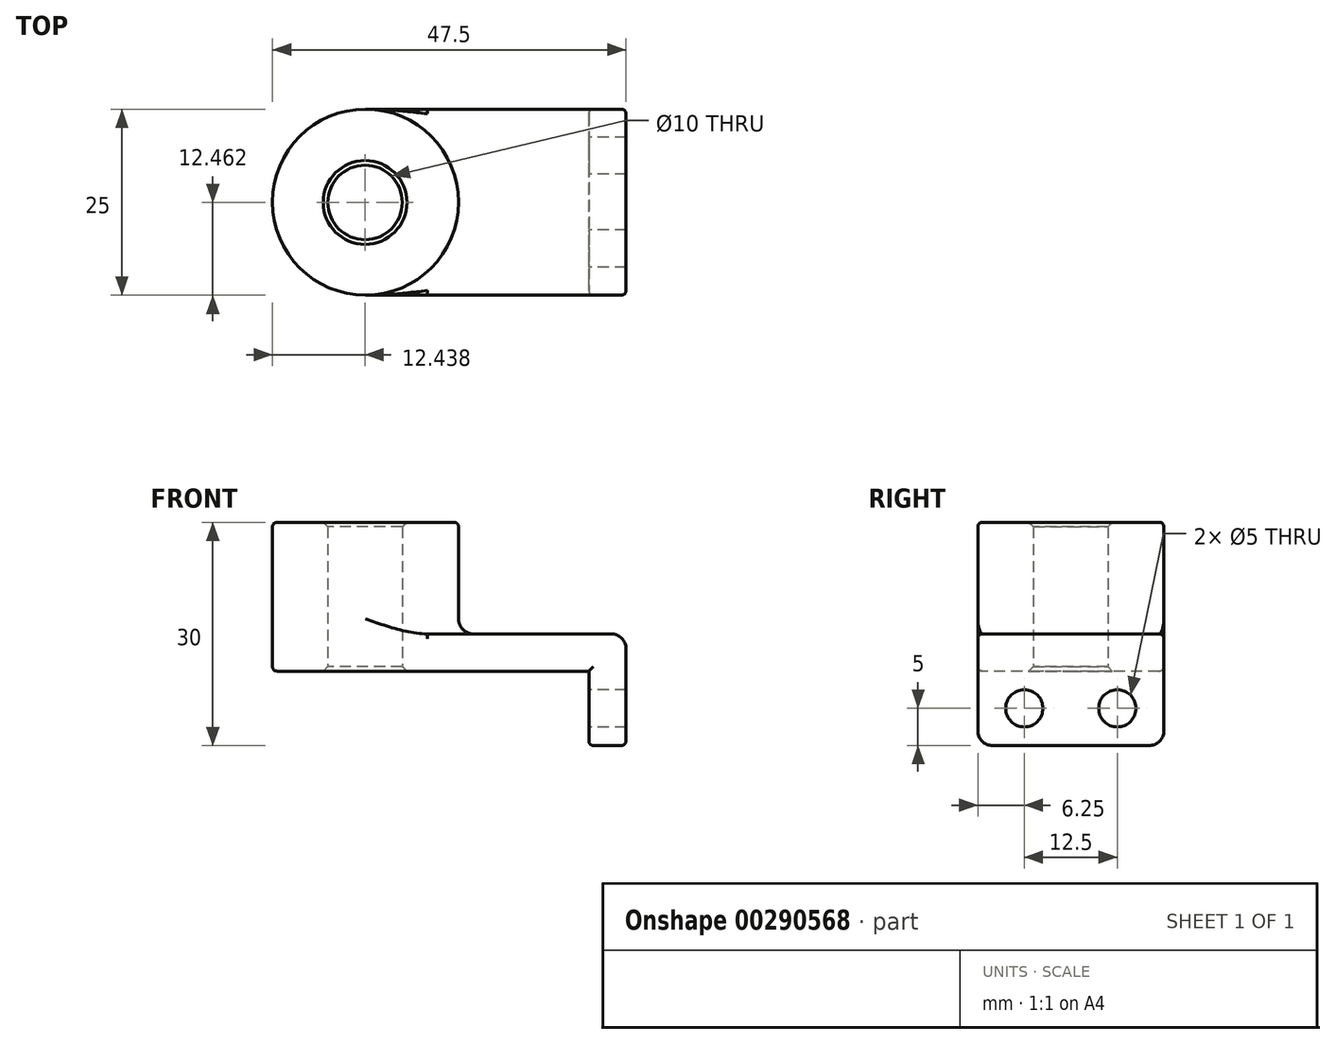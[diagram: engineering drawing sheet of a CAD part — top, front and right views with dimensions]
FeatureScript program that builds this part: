
annotation { "Feature Type Name" : "Feature", "Feature Type Description" : "" }
export const myFeature = defineFeature(function(context is Context, id is Id, definition is map)
    precondition{}
    {
        {
            var Q0;
            Q0=qCreatedBy(makeId("Top.planeOp"),FACE);
            var sketch = newSketch(context, id + "F0", { "sketchPlane" : qUnion([Q0])});
            skLineSegment(sketch, "E0.bottom", {"start": v(15, 12.5) * mm, "end": v(-15, 12.5) * mm});
            skLineSegment(sketch, "E0.top", {"start": v(15, -12.5) * mm, "end": v(-15, -12.5) * mm});
            skLineSegment(sketch, "E0.left", {"start": v(15, 12.5) * mm, "end": v(15, -12.5) * mm});
            skLineSegment(sketch, "E0.right", {"start": v(-15, 12.5) * mm, "end": v(-15, -12.5) * mm});
            skPoint(sketch, "E0.middle", {"position": v(0, 0) * mm});
            skCircle(sketch, "E1", {"center": v(-15, 0) * mm, "radius": 12.5 * mm});
            skCircle(sketch, "E2", {"center": v(-15.06, -0.04) * mm, "radius": 5 * mm});
            skSolve(sketch);
        }
        {
            var Q0;
            {var subQ1=sQuery(id+"F0.wireOp",EDGE,"E0.right");var subQ3=sQuery(id+"F0.wireOp",EDGE,"E2");var subQ4=makeQuery(id+"F0.imprint","INTERSECT",VERTEX,{"disambiguationData":[OD(0.0)],"derivedFrom":[subQ1,subQ3]});Q0=makeQuery(id+"F0.imprint","IMPRINT",FACE,{"disambiguationData":[TD([[makeQuery(id+"F0.imprint","IMPRINT",EDGE,{"disambiguationData":[TD([[subQ4,-1.0]])],"derivedFrom":subQ3}),-1.0]])]});}
            var Q1;
            {var subQ1=sQuery(id+"F0.wireOp",EDGE,"E0.right");var subQ3=sQuery(id+"F0.wireOp",EDGE,"E2");var subQ4=makeQuery(id+"F0.imprint","INTERSECT",VERTEX,{"disambiguationData":[OD(0.0)],"derivedFrom":[subQ1,subQ3]});Q1=makeQuery(id+"F0.imprint","IMPRINT",FACE,{"disambiguationData":[TD([[makeQuery(id+"F0.imprint","IMPRINT",EDGE,{"disambiguationData":[TD([[subQ4,1.0]])],"derivedFrom":subQ3}),-1.0]])]});}
            var Q2;
            {var subQ0=sQuery(id+"F0.wireOp",EDGE,"E0.bottom");Q2=makeQuery(id+"F0.imprint","IMPRINT",FACE,{"disambiguationData":[TD([[makeQuery(id+"F0.imprint","IMPRINT",EDGE,{"derivedFrom":subQ0}),1.0]])]});}
            extrude(context, id + "F1", {"entities" : qUnion([Q0, Q1, Q2]), "depth" : 5 * mm});
        }
        {
            var Q0;
            {var subQ1=sQuery(id+"F0.wireOp",EDGE,"E0.right");var subQ3=sQuery(id+"F0.wireOp",EDGE,"E2");var subQ4=makeQuery(id+"F0.imprint","INTERSECT",VERTEX,{"disambiguationData":[OD(0.0)],"derivedFrom":[subQ1,subQ3]});Q0=makeQuery(id+"F0.imprint","IMPRINT",FACE,{"disambiguationData":[TD([[makeQuery(id+"F0.imprint","IMPRINT",EDGE,{"disambiguationData":[TD([[subQ4,1.0]])],"derivedFrom":subQ3}),-1.0]])]});}
            var Q1;
            {var subQ1=sQuery(id+"F0.wireOp",EDGE,"E0.right");var subQ3=sQuery(id+"F0.wireOp",EDGE,"E2");var subQ4=makeQuery(id+"F0.imprint","INTERSECT",VERTEX,{"disambiguationData":[OD(0.0)],"derivedFrom":[subQ1,subQ3]});Q1=makeQuery(id+"F0.imprint","IMPRINT",FACE,{"disambiguationData":[TD([[makeQuery(id+"F0.imprint","IMPRINT",EDGE,{"disambiguationData":[TD([[subQ4,-1.0]])],"derivedFrom":subQ3}),-1.0]])]});}
            extrude(context, id + "F2", {"entities" : qUnion([Q0, Q1]), "operationType" : NewBodyOperationType.ADD, "depth" : 20 * mm});
        }
        {
            var Q0;
            Q0=makeQuery(id+"F1.opExtrude","SWEPT_FACE",FACE,{"disambiguationData":[OSD([sQuery(id+"F0.wireOp",EDGE,"E0.left")])]});
            var sketch = newSketch(context, id + "F3", { "sketchPlane" : qUnion([Q0])});
            skPoint(sketch, "E3.oppositeSnap0", {"position": v(12.5, 2.5) * mm});
            skLineSegment(sketch, "E3.bottom", {"start": v(-12.5, 5) * mm, "end": v(12.5, 5) * mm});
            skLineSegment(sketch, "E3.top", {"start": v(-12.5, -10) * mm, "end": v(12.5, -10) * mm});
            skLineSegment(sketch, "E3.left", {"start": v(-12.5, 5) * mm, "end": v(-12.5, -10) * mm});
            skLineSegment(sketch, "E3.right", {"start": v(12.5, 5) * mm, "end": v(12.5, -10) * mm});
            skLineSegment(sketch, "E4", {"start": v(0, 5) * mm, "end": v(0, -10) * mm});
            skPoint(sketch, "E4.startSnap0", {"position": v(0, 5) * mm});
            skPoint(sketch, "E4.startSnap1", {"position": v(0, 5) * mm});
            skPoint(sketch, "E4.endSnap0", {"position": v(0, 5) * mm});
            skCircle(sketch, "E5", {"center": v(-6.25, -5) * mm, "radius": 2.5 * mm});
            skCircle(sketch, "E6.MirrorC", {"center": v(6.25, -5) * mm, "radius": 2.5 * mm});
            skSolve(sketch);
        }
        {
            var Q0;
            {var subQ5=sQuery(id+"F3.wireOp",EDGE,"E3.top");var subQ8=sQuery(id+"F3.wireOp",EDGE,"E3.left");var subQ10=makeQuery(id+"F3.imprint","INTERSECT",VERTEX,{"derivedFrom":[subQ5,subQ8]});Q0=makeQuery(id+"F3.imprint","IMPRINT",FACE,{"disambiguationData":[TD([[makeQuery(id+"F3.imprint","IMPRINT",EDGE,{"disambiguationData":[TD([[subQ10,-1.0]])],"derivedFrom":subQ5}),1.0]])]});}
            var Q1;
            {var subQ1=sQuery(id+"F3.wireOp",EDGE,"E3.bottom");var subQ8=sQuery(id+"F3.wireOp",EDGE,"E3.left");var subQ10=makeQuery(id+"F3.imprint","INTERSECT",VERTEX,{"derivedFrom":[subQ1,subQ8]});Q1=makeQuery(id+"F3.imprint","IMPRINT",FACE,{"disambiguationData":[TD([[makeQuery(id+"F3.imprint","IMPRINT",EDGE,{"disambiguationData":[TD([[subQ10,1.0]])],"derivedFrom":subQ1}),1.0]])]});}
            var Q2;
            {var subQ5=sQuery(id+"F3.wireOp",EDGE,"E3.bottom");var subQ8=sQuery(id+"F3.wireOp",EDGE,"E3.right");var subQ10=makeQuery(id+"F3.imprint","INTERSECT",VERTEX,{"derivedFrom":[subQ5,subQ8]});Q2=makeQuery(id+"F3.imprint","IMPRINT",FACE,{"disambiguationData":[TD([[makeQuery(id+"F3.imprint","IMPRINT",EDGE,{"disambiguationData":[TD([[subQ10,-1.0]])],"derivedFrom":subQ5}),1.0]])]});}
            var Q3;
            {var subQ5=sQuery(id+"F3.wireOp",EDGE,"E3.top");var subQ8=sQuery(id+"F3.wireOp",EDGE,"E3.right");var subQ10=makeQuery(id+"F3.imprint","INTERSECT",VERTEX,{"derivedFrom":[subQ5,subQ8]});Q3=makeQuery(id+"F3.imprint","IMPRINT",FACE,{"disambiguationData":[TD([[makeQuery(id+"F3.imprint","IMPRINT",EDGE,{"disambiguationData":[TD([[subQ10,1.0]])],"derivedFrom":subQ5}),1.0]])]});}
            extrude(context, id + "F4", {"entities" : qUnion([Q0, Q1, Q2, Q3]), "operationType" : NewBodyOperationType.ADD, "depth" : 5 * mm});
        }
        {
            var Q0;
            {var subQ0=sQuery(id+"F0.wireOp",EDGE,"E1");Q0=makeQuery(id+"F2.boolean.opBoolean","INTERSECT",EDGE,{"derivedFrom":[makeQuery(id+"F1.opExtrude","CAP_FACE",FACE,{"disambiguationData":[OSD([sQuery(id+"F0.wireOp",EDGE,"E0.bottom"),sQuery(id+"F0.wireOp",EDGE,"E0.top"),sQuery(id+"F0.wireOp",EDGE,"E0.left"),subQ0,sQuery(id+"F0.wireOp",EDGE,"E2")])],"isStart":false}),makeQuery(id+"F2.opExtrude","SWEPT_FACE",FACE,{"disambiguationData":[OSD([subQ0])]})]});}
            var Q1;
            Q1=makeQuery(id+"F4.opExtrude","CAP_EDGE",EDGE,{"disambiguationData":[OSD([sQuery(id+"F3.wireOp",EDGE,"E3.bottom")])],"isStart":false});
            var Q2;
            Q2=makeQuery(id+"F4.opExtrude","SWEPT_EDGE",EDGE,{"disambiguationData":[OSD([sQuery(id+"F3.wireOp",EDGE,"E3.top"),sQuery(id+"F3.wireOp",EDGE,"E3.left")])]});
            var Q3;
            Q3=makeQuery(id+"F4.opExtrude","SWEPT_EDGE",EDGE,{"disambiguationData":[OSD([sQuery(id+"F3.wireOp",EDGE,"E3.top"),sQuery(id+"F3.wireOp",EDGE,"E3.right")])]});
            var Q4;
            Q4=makeQuery(id+"F1.opExtrude","CAP_EDGE",EDGE,{"disambiguationData":[OSD([sQuery(id+"F0.wireOp",EDGE,"E0.left")])],"isStart":true});
            fillet(context, id + "F5", {"entities" : qUnion([Q0, Q1, Q2, Q3, Q4]), "radius" : 2 * mm, "tangentPropagation" : true, "allowEdgeOverflow" : false});
        }
        {
            var Q0;
            Q0=makeQuery(id+"F4.boolean.opBoolean","MERGE",EDGE,{"derivedFrom":[makeQuery(id+"F1.opExtrude","CAP_EDGE",EDGE,{"disambiguationData":[OSD([sQuery(id+"F0.wireOp",EDGE,"E0.top")])],"isStart":false}),makeQuery(id+"F4.opExtrude","SWEPT_EDGE",EDGE,{"disambiguationData":[OSD([sQuery(id+"F3.wireOp",EDGE,"E3.bottom"),sQuery(id+"F3.wireOp",EDGE,"E3.left")])]})]});
            var Q1;
            Q1=makeQuery(id+"F1.opExtrude","CAP_EDGE",EDGE,{"disambiguationData":[OSD([sQuery(id+"F0.wireOp",EDGE,"E0.top")])],"isStart":true});
            var Q2;
            Q2=makeQuery(id+"F4.opExtrude","CAP_EDGE",EDGE,{"disambiguationData":[OSD([sQuery(id+"F3.wireOp",EDGE,"E3.left")])],"isStart":false});
            var Q3;
            Q3=makeQuery(id+"F5.opFillet","BLEND_EDGE",EDGE,{"blendedFrom":[makeQuery(id+"F4.opExtrude","CAP_EDGE",EDGE,{"disambiguationData":[OSD([sQuery(id+"F3.wireOp",EDGE,"E3.bottom")])],"isStart":false}),makeQuery(id+"F4.boolean.opBoolean","MERGE",FACE,{"derivedFrom":[makeQuery(id+"F1.opExtrude","SWEPT_FACE",FACE,{"disambiguationData":[OSD([sQuery(id+"F0.wireOp",EDGE,"E0.top")])]}),makeQuery(id+"F4.opExtrude","SWEPT_FACE",FACE,{"disambiguationData":[OSD([sQuery(id+"F3.wireOp",EDGE,"E3.left")])]})]})],"blendedInto":[makeQuery(id+"F4.boolean.opBoolean","MERGE",FACE,{"derivedFrom":[makeQuery(id+"F1.opExtrude","SWEPT_FACE",FACE,{"disambiguationData":[OSD([sQuery(id+"F0.wireOp",EDGE,"E0.top")])]}),makeQuery(id+"F4.opExtrude","SWEPT_FACE",FACE,{"disambiguationData":[OSD([sQuery(id+"F3.wireOp",EDGE,"E3.left")])]})]})]});
            var Q4;
            Q4=makeQuery(id+"F4.opExtrude","CAP_EDGE",EDGE,{"disambiguationData":[OSD([sQuery(id+"F3.wireOp",EDGE,"E3.left")])],"isStart":true});
            var Q5;
            Q5=makeQuery(id+"F5.opFillet","BLEND_EDGE",EDGE,{"blendedFrom":[makeQuery(id+"F1.opExtrude","CAP_EDGE",EDGE,{"disambiguationData":[OSD([sQuery(id+"F0.wireOp",EDGE,"E0.left")])],"isStart":true}),makeQuery(id+"F4.boolean.opBoolean","MERGE",FACE,{"derivedFrom":[makeQuery(id+"F1.opExtrude","SWEPT_FACE",FACE,{"disambiguationData":[OSD([sQuery(id+"F0.wireOp",EDGE,"E0.top")])]}),makeQuery(id+"F4.opExtrude","SWEPT_FACE",FACE,{"disambiguationData":[OSD([sQuery(id+"F3.wireOp",EDGE,"E3.left")])]})]})],"blendedInto":[makeQuery(id+"F4.boolean.opBoolean","MERGE",FACE,{"derivedFrom":[makeQuery(id+"F1.opExtrude","SWEPT_FACE",FACE,{"disambiguationData":[OSD([sQuery(id+"F0.wireOp",EDGE,"E0.top")])]}),makeQuery(id+"F4.opExtrude","SWEPT_FACE",FACE,{"disambiguationData":[OSD([sQuery(id+"F3.wireOp",EDGE,"E3.left")])]})]})]});
            var Q6;
            Q6=makeQuery(id+"F2.opExtrude","CAP_EDGE",EDGE,{"disambiguationData":[OSD([sQuery(id+"F0.wireOp",EDGE,"E1")])],"isStart":false});
            fillet(context, id + "F6", {"entities" : qUnion([Q0, Q1, Q2, Q3, Q4, Q5, Q6]), "radius" : 0.62 * mm, "tangentPropagation" : true, "allowEdgeOverflow" : false});
        }
        {
            var Q0;
            {var subQ0=sQuery(id+"F0.wireOp",EDGE,"E2");Q0=makeQuery(id+"F2.boolean.opBoolean","MERGE",FACE,{"derivedFrom":[makeQuery(id+"F1.opExtrude","SWEPT_FACE",FACE,{"disambiguationData":[OSD([subQ0])]}),makeQuery(id+"F2.opExtrude","SWEPT_FACE",FACE,{"disambiguationData":[OSD([subQ0])]})]});}
            chamfer(context, id + "F7", {"entities" : qUnion([Q0]), "width" : 0.62 * mm, "tangentPropagation" : true});
        }
    });
